FREECAD ASSEMBLY — COMPONENT RECIPES ("Robot")

This assembly document has 5 components, labeled P0..P4 below (a component is one placed body or linked part). 1 of them carries a construction recipe — the FreeCAD feature program that regenerates the part from scratch, quoted from this document or its linked companion documents; the rest are supplied as boundary geometry only. No exploded tour is included for this assembly.
COMPONENT P0 — geometry summary ("DisplayGroup"; no construction recipe available for this part):
  bounding box: 156.0 x 97.0 x 45.0 mm
  tessellated surface: 7,056 triangles
  volume: 191994 mm^3 (28% of its bounding box)
  symmetry: mirror-symmetric across its x mid-plane
COMPONENT P1 — geometry summary ("BodyHolder001"; no construction recipe available for this part):
  bounding box: 90.5 x 83.0 x 64.0 mm
  tessellated surface: 4,908 triangles
  volume: 135069 mm^3 (28% of its bounding box)
  symmetry: mirror-symmetric across its x mid-plane
COMPONENT P2 — geometry summary ("SecondShaft"; no construction recipe available for this part):
  bounding box: 289.3 x 196.0 x 82.9 mm
  tessellated surface: 50,792 triangles
  volume: 322852 mm^3 (7% of its bounding box)
COMPONENT P3 — geometry summary ("RobotBody"; no construction recipe available for this part):
  bounding box: 265.1 x 250.4 x 179.9 mm
  tessellated surface: 350,744 triangles
  volume: 429831 mm^3 (4% of its bounding box)
COMPONENT P4 — recipe-attached ("WoodenChessBoard", a linked part whose construction recipe lives in a companion FreeCAD document of the same project; that document's serialized recipe follows).
Construction recipe (the companion document, serialized — sketch geometry with constraints, then the solid features built on it; lengths are millimeters unless a unit is written):

FCSTD DOCUMENT  (FreeCAD 1.0R39319 (Git))
Label: ChessBoard
License: All rights reserved
LicenseURL: https://en.wikipedia.org/wiki/All_rights_reserved
objects: Sketcher::SketchObject×19, PartDesign::Pocket×10, PartDesign::Pad×8, PartDesign::Body×6, App::LinkGroup×3, App::Link×3, PartDesign::Hole×2, Part::Mirroring×2, Image::ImagePlane×1
note: 106 computed .brp shape members not serialized (recipe doc carries the construction recipe); baked Part::Feature solids carry a one-line shape summary decoded from their .brp
EXTERNAL_REF file=NavigationBoard.FCStd obj=LinkGroup
EXTERNAL_REF file=SnapLock.FCStd obj=LinkGroup
EXTERNAL_REF file=SnapLock.FCStd obj=LinkGroup001

FEATURE [Sketcher::SketchObject] Sketch
  ArcFitTolerance = 1e-06
  AttachmentSupport = -> [XY_Plane]
  FullyConstrained = true
  MakeInternals = false
  MapMode = 5
  sketch-geometry (5):
    g0: LineSegment StartX=-250 StartY=-150 StartZ=0 EndX=250 EndY=-150 EndZ=0
    g1: LineSegment StartX=250 StartY=-150 StartZ=0 EndX=250 EndY=150 EndZ=0
    g2: LineSegment StartX=250 StartY=150 StartZ=0 EndX=-250 EndY=150 EndZ=0
    g3: LineSegment StartX=-250 StartY=150 StartZ=0 EndX=-250 EndY=-150 EndZ=0
    g4: GeomPoint [constr] X=0 Y=0 Z=0
  constraints (12):
    c: Coincident(g0,g1)
    c: Coincident(g1,g2)
    c: Coincident(g2,g3)
    c: Coincident(g3,g0)
    c: Horizontal(g0)
    c: Horizontal(g2)
    c: Vertical(g1)
    c: Vertical(g3)
    c: Symmetric(g2,g0,g4)
    c: Distance(g1,g3) = 500
    c: Distance(g0,g2) = 300
    c: Coincident(g4,g-1)
FEATURE [Image::ImagePlane] ChessBoard
  Placement = pos=(0,0,30) rot=(0,0,1;0rad)
  XSize = 500.127
  YSize = 300.144
FEATURE [PartDesign::Pad] Pad
  Direction = (0,0,1)
  Length = 5
  Length2 = 10
  Profile = -> Sketch
  ReferenceAxis = -> Sketch [N_Axis]
  Refine = true
  Suppressed = false
  Type = 0
FEATURE [Sketcher::SketchObject] Sketch001
  ArcFitTolerance = 1e-06
  AttachmentSupport = -> [XY_Plane001]
  FullyConstrained = true
  MakeInternals = false
  MapMode = 5
  sketch-geometry (5):
    g0: LineSegment StartX=-150 StartY=-150 StartZ=0 EndX=150 EndY=-150 EndZ=0
    g1: LineSegment StartX=150 StartY=-150 StartZ=0 EndX=150 EndY=150 EndZ=0
    g2: LineSegment StartX=150 StartY=150 StartZ=0 EndX=-150 EndY=150 EndZ=0
    g3: LineSegment StartX=-150 StartY=150 StartZ=0 EndX=-150 EndY=-150 EndZ=0
    g4: GeomPoint [constr] X=0 Y=0 Z=0
  constraints (12):
    c: Coincident(g0,g1)
    c: Coincident(g1,g2)
    c: Coincident(g2,g3)
    c: Coincident(g3,g0)
    c: Horizontal(g0)
    c: Horizontal(g2)
    c: Vertical(g1)
    c: Vertical(g3)
    c: Symmetric(g2,g0,g4)
    c: Distance(g1,g3) = 300
    c: Distance(g0,g2) = 300
    c: Coincident(g4,g-1)
FEATURE [PartDesign::Pad] Pad001
  Direction = (0,0,1)
  Length = 5
  Length2 = 10
  Profile = -> Sketch001
  ReferenceAxis = -> Sketch001 [N_Axis]
  Refine = true
  Suppressed = false
  Type = 0
FEATURE [PartDesign::Body] Body001  label="MainBoard"
  AllowCompound = false
  Group = -> [Sketch001,Pad001]
  Origin = -> Origin001
  Placement = pos=(0,0,25) rot=(0,0,1;0rad)
  Tip = -> Pad001
FEATURE [Sketcher::SketchObject] Sketch002
  ArcFitTolerance = 1e-06
  AttachmentSupport = -> [XY_Plane002]
  FullyConstrained = true
  MakeInternals = false
  MapMode = 5
  sketch-geometry (4):
    g0: LineSegment StartX=0 StartY=0 StartZ=0 EndX=0 EndY=-300 EndZ=0
    g1: LineSegment StartX=0 StartY=-300 StartZ=0 EndX=100 EndY=-300 EndZ=0
    g2: LineSegment StartX=100 StartY=-300 StartZ=0 EndX=100 EndY=0 EndZ=0
    g3: LineSegment StartX=100 StartY=0 StartZ=0 EndX=0 EndY=0 EndZ=0
  constraints (11):
    c: Coincident(g0,g1)
    c: Coincident(g1,g2)
    c: Coincident(g2,g3)
    c: Coincident(g3,g0)
    c: Vertical(g0)
    c: Vertical(g2)
    c: Horizontal(g1)
    c: Horizontal(g3)
    c: Distance(g0,g2) = 100
    c: Distance(g1,g3) = 300
    c: Coincident(g0,g-1)
FEATURE [PartDesign::Pad] Pad002
  Direction = (0,0,1)
  Length = 5
  Length2 = 10
  Profile = -> Sketch002
  ReferenceAxis = -> Sketch002 [N_Axis]
  Refine = true
  Suppressed = false
  Type = 0
FEATURE [PartDesign::Body] Body002  label="DropLeft"
  AllowCompound = false
  Group = -> [Sketch002,Pad002]
  Origin = -> Origin002
  Placement = pos=(-250,150,25) rot=(0,0,1;0rad)
  Tip = -> Pad002
FEATURE [Sketcher::SketchObject] Sketch003
  ArcFitTolerance = 1e-06
  AttachmentSupport = -> [XY_Plane003]
  FullyConstrained = true
  MakeInternals = false
  MapMode = 5
  sketch-geometry (4):
    g0: LineSegment StartX=0 StartY=0 StartZ=0 EndX=-100 EndY=0 EndZ=0
    g1: LineSegment StartX=-100 StartY=0 StartZ=0 EndX=-100 EndY=-300 EndZ=0
    g2: LineSegment StartX=-100 StartY=-300 StartZ=0 EndX=0 EndY=-300 EndZ=0
    g3: LineSegment StartX=0 StartY=-300 StartZ=0 EndX=0 EndY=0 EndZ=0
  constraints (11):
    c: Coincident(g0,g1)
    c: Coincident(g1,g2)
    c: Coincident(g2,g3)
    c: Coincident(g3,g0)
    c: Horizontal(g0)
    c: Horizontal(g2)
    c: Vertical(g1)
    c: Vertical(g3)
    c: Distance(g1,g3) = 100
    c: Distance(g0,g2) = 300
    c: Coincident(g0,g-1)
FEATURE [PartDesign::Pad] Pad003
  Direction = (0,0,1)
  Length = 5
  Length2 = 10
  Profile = -> Sketch003
  ReferenceAxis = -> Sketch003 [N_Axis]
  Refine = true
  Suppressed = false
  Type = 0
FEATURE [PartDesign::Body] Body003  label="DropRight"
  AllowCompound = false
  Group = -> [Sketch003,Pad003]
  Origin = -> Origin003
  Placement = pos=(250,150,25) rot=(0,0,1;0rad)
  Tip = -> Pad003
FEATURE [Sketcher::SketchObject] Sketch004
  ArcFitTolerance = 1e-06
  AttachmentSupport = -> [XY_Plane004]
  FullyConstrained = false
  MakeInternals = false
  MapMode = 5
  sketch-geometry (13):
    g0: LineSegment StartX=0 StartY=40 StartZ=0 EndX=0 EndY=0 EndZ=0
    g1: LineSegment StartX=0 StartY=0 StartZ=0 EndX=160 EndY=0 EndZ=0
    g2: LineSegment StartX=0 StartY=40 StartZ=0 EndX=10 EndY=40 EndZ=0
    g3: LineSegment StartX=10 StartY=40 StartZ=0 EndX=10 EndY=30 EndZ=0
    g4: ArcOfCircle CenterX=30 CenterY=30 CenterZ=0 NormalX=0 NormalY=0 NormalZ=1 AngleXU=0 Radius=20 StartAngle=3.14159 EndAngle=4.71239
    g5: LineSegment StartX=90 StartY=42.0946 StartZ=0 EndX=115 EndY=42.0946 EndZ=0
    g6: LineSegment StartX=115 StartY=42.0946 StartZ=0 EndX=115 EndY=25 EndZ=0
    g7: LineSegment StartX=90 StartY=42.0946 StartZ=0 EndX=90 EndY=20 EndZ=0
    g8: LineSegment StartX=30 StartY=10 StartZ=0 EndX=80 EndY=10 EndZ=0
    g9: ArcOfCircle CenterX=125 CenterY=25 CenterZ=0 NormalX=0 NormalY=0 NormalZ=1 AngleXU=0 Radius=10 StartAngle=3.14159 EndAngle=4.71239
    g10: ArcOfCircle CenterX=80 CenterY=20 CenterZ=0 NormalX=0 NormalY=0 NormalZ=1 AngleXU=0 Radius=10 StartAngle=4.71239 EndAngle=6.28319
    g11: LineSegment StartX=125 StartY=15 StartZ=0 EndX=160 EndY=15 EndZ=0
    g12: LineSegment StartX=160 StartY=15 StartZ=0 EndX=160 EndY=0 EndZ=0
  constraints (38):
    c: PointOnObject(g0,g-2)
    c: Coincident(g0,g-1)
    c: Coincident(g0,g1)
    c: Coincident(g0,g2)
    c: Horizontal(g2)
    c: Coincident(g2,g3)
    c: Vertical(g3)
    c: Coincident(g4,g3)
    c: Vertical(g4,g4)
    c: Horizontal(g4,g3)
    c: Radius(g4) = 20
    c: DistanceY(g1,g9) = 15
    c: Distance(g2,g2) = 10
    c: DistanceY(g0,g0) = 40
    c: Horizontal(g5)
    c: Coincident(g5,g6)
    c: Vertical(g6)
    c: Coincident(g5,g7)
    c: Vertical(g7)
    c: Tangent(g4,g8) = -1.5708
    c: Coincident(g9,g6)
    c: Coincident(g10,g7)
    c: Coincident(g10,g8)
    c: Distance(g1,g8) = 10
    c: Radius(g10) = 10
    c: Vertical(g10,g8)
    c: Horizontal(g10,g7)
    c: Radius(g9) = 10
    c: Vertical(g9,g9)
    c: Horizontal(g9,g6)
    c: DistanceX(g-1,g10) = 80
    c: Tangent(g9,g11) = -1.5708
    c: Coincident(g11,g12)
    c: Vertical(g12)
    c: Coincident(g1,g12)
    c: Horizontal(g1)
    c: Distance(g-2,g12) = 160
    c: DistanceX(g5,g5) = 25
FEATURE [PartDesign::Pad] Pad004
  Direction = (0,0,1)
  Length = 29
  Length2 = 10
  Profile = -> Sketch004
  ReferenceAxis = -> Sketch004 [N_Axis]
  Refine = true
  Suppressed = false
  Type = 0
FEATURE [App::LinkGroup] LinkGroup002  label="TopBoard"
  ElementList = -> [Body001,Body002,Body003,ChessBoard]
  LinkMode = 0
  Placement = pos=(0,0,-1) rot=(0,0,1;0rad)
FEATURE [Sketcher::SketchObject] Sketch005
  ArcFitTolerance = 1e-06
  AttachmentSupport = -> [Pad]
  ExternalGeometry = -> [Sketch]
  FullyConstrained = false
  MakeInternals = false
  MapMode = 5
  Placement = pos=(0,0,0) rot=(1,0,0;3.14159rad)
  sketch-geometry (4):
    g0: LineSegment StartX=-92 StartY=-50 StartZ=0 EndX=-92 EndY=-193.39 EndZ=0
    g1: LineSegment StartX=-92 StartY=-193.39 StartZ=0 EndX=92 EndY=-193.39 EndZ=0
    g2: LineSegment StartX=92 StartY=-193.39 StartZ=0 EndX=92 EndY=-50 EndZ=0
    g3: LineSegment StartX=92 StartY=-50 StartZ=0 EndX=-92 EndY=-50 EndZ=0
  constraints (11):
    c: Coincident(g0,g1)
    c: Coincident(g1,g2)
    c: Coincident(g2,g3)
    c: Coincident(g3,g0)
    c: Vertical(g0)
    c: Vertical(g2)
    c: Horizontal(g1)
    c: Horizontal(g3)
    c: Distance(g-2,g2) = 92
    c: Distance(g-2,g0) = 92
    c: Distance(g-3,g3) = 100
FEATURE [PartDesign::Pocket] Pocket
  BaseFeature = -> Pad
  Direction = (0,0,1)
  Length = 5
  Length2 = 5
  Profile = -> Sketch005
  ReferenceAxis = -> Sketch005 [N_Axis]
  Refine = true
  Suppressed = false
  Type = 0
FEATURE [PartDesign::Body] Body  label="Bottom"
  AllowCompound = false
  Group = -> [Sketch,Pad,Sketch005,Pocket]
  Origin = -> Origin
  Tip = -> Pocket
FEATURE [Sketcher::SketchObject] Sketch006
  ArcFitTolerance = 1e-06
  AttachmentSupport = -> [Pad004]
  FullyConstrained = false
  MakeInternals = false
  MapMode = 5
  Placement = pos=(0,0,29) rot=(0,0,1;0rad)
  sketch-geometry (6):
    g0: LineSegment StartX=5 StartY=45 StartZ=0 EndX=5 EndY=5 EndZ=0
    g1: LineSegment StartX=5 StartY=5 StartZ=0 EndX=100 EndY=5 EndZ=0
    g2: LineSegment StartX=275.375 StartY=45 StartZ=0 EndX=5 EndY=45 EndZ=0
    g3: LineSegment StartX=100 StartY=5 StartZ=0 EndX=100 EndY=-8.02974 EndZ=0
    g4: LineSegment StartX=100 StartY=-8.02974 StartZ=0 EndX=275.375 EndY=-8.02974 EndZ=0
    g5: LineSegment StartX=275.375 StartY=45 StartZ=0 EndX=275.375 EndY=-8.02974 EndZ=0
  constraints (16):
    c: Coincident(g0,g1)
    c: Coincident(g2,g0)
    c: Vertical(g0)
    c: Horizontal(g1)
    c: Horizontal(g2)
    c: Distance(g-2,g0) = 5
    c: Distance(g-1,g1) = 5
    c: DistanceY(g0,g0) = 40
    c: Vertical(g3)
    c: Coincident(g3,g4)
    c: Horizontal(g4)
    c: Coincident(g1,g3)
    c: Coincident(g5,g2)
    c: Coincident(g5,g4)
    c: Vertical(g5)
    c: Distance(g-2,g3) = 100
FEATURE [PartDesign::Pocket] Pocket001
  BaseFeature = -> Pad004
  Direction = (0,0,-1)
  Length = 5
  Length2 = 5
  Profile = -> Sketch006
  ReferenceAxis = -> Sketch006 [N_Axis]
  Refine = true
  Suppressed = false
  Type = 0
FEATURE [Sketcher::SketchObject] Sketch007
  ArcFitTolerance = 1e-06
  AttachmentSupport = -> [Pocket001]
  FullyConstrained = false
  MakeInternals = false
  MapMode = 5
  Placement = pos=(0,0,0) rot=(1,0,0;3.14159rad)
  sketch-geometry (6):
    g0: LineSegment StartX=5 StartY=-5 StartZ=0 EndX=5 EndY=-45 EndZ=0
    g1: LineSegment StartX=5 StartY=-45 StartZ=0 EndX=160 EndY=-45 EndZ=0
    g2: LineSegment StartX=45 StartY=-5 StartZ=0 EndX=5 EndY=-5 EndZ=0
    g3: LineSegment StartX=45 StartY=-5 StartZ=0 EndX=45 EndY=8.54607 EndZ=0
    g4: LineSegment StartX=45 StartY=8.54607 StartZ=0 EndX=160 EndY=8.54607 EndZ=0
    g5: LineSegment StartX=160 StartY=8.54607 StartZ=0 EndX=160 EndY=-45 EndZ=0
  constraints (17):
    c: Coincident(g0,g1)
    c: Coincident(g2,g0)
    c: Vertical(g0)
    c: Horizontal(g1)
    c: Horizontal(g2)
    c: Distance(g-1,g2) = 5
    c: Distance(g-2,g0) = 5
    c: DistanceY(g0,g0) = 40
    c: Coincident(g2,g3)
    c: Vertical(g3)
    c: Coincident(g3,g4)
    c: Horizontal(g4)
    c: Coincident(g4,g5)
    c: Coincident(g5,g1)
    c: Vertical(g5)
    c: DistanceX(g0,g2) = 40
    c: Distance(g1,g-2) = 160
FEATURE [PartDesign::Pocket] Pocket002
  BaseFeature = -> Pocket001
  Direction = (0,0,1)
  Length = 5
  Length2 = 5
  Profile = -> Sketch007
  ReferenceAxis = -> Sketch007 [N_Axis]
  Refine = true
  Suppressed = false
  Type = 0
FEATURE [Sketcher::SketchObject] Sketch008
  ArcFitTolerance = 1e-06
  AttachmentSupport = -> [Pocket002]
  ExternalGeometry = -> [Pocket002]
  FullyConstrained = true
  MakeInternals = false
  MapMode = 5
  Placement = pos=(0,0,24) rot=(0,0,1;0rad)
  sketch-geometry (1):
    g0: Circle CenterX=110 CenterY=10 CenterZ=0 NormalX=0 NormalY=0 NormalZ=1 AngleXU=0 Radius=5
  constraints (3):
    c: Diameter(g0) = 10
    c: Distance(g0,g-1) = 10
    c: DistanceX(g-3,g0) = 10
FEATURE [PartDesign::Pocket] Pocket003
  BaseFeature = -> Pocket002
  Direction = (0,0,-1)
  Length = 10
  Length2 = 5
  Profile = -> Sketch008
  ReferenceAxis = -> Sketch008 [N_Axis]
  Refine = true
  Suppressed = false
  Type = 0
FEATURE [Sketcher::SketchObject] Sketch009
  ArcFitTolerance = 1e-06
  AttachmentSupport = -> [XY_Plane005]
  FullyConstrained = false
  MakeInternals = false
  MapMode = 5
  sketch-geometry (13):
    g0: LineSegment StartX=0 StartY=40 StartZ=0 EndX=0 EndY=0 EndZ=0
    g1: LineSegment StartX=0 StartY=0 StartZ=0 EndX=160 EndY=0 EndZ=0
    g2: LineSegment StartX=0 StartY=40 StartZ=0 EndX=10 EndY=40 EndZ=0
    g3: LineSegment StartX=10 StartY=40 StartZ=0 EndX=10 EndY=30 EndZ=0
    g4: ArcOfCircle CenterX=30 CenterY=30 CenterZ=0 NormalX=0 NormalY=0 NormalZ=1 AngleXU=0 Radius=20 StartAngle=3.14159 EndAngle=4.71239
    g5: LineSegment StartX=90 StartY=42.0946 StartZ=0 EndX=115 EndY=42.0946 EndZ=0
    g6: LineSegment StartX=115 StartY=42.0946 StartZ=0 EndX=115 EndY=25 EndZ=0
    g7: LineSegment StartX=90 StartY=42.0946 StartZ=0 EndX=90 EndY=20 EndZ=0
    g8: LineSegment StartX=30 StartY=10 StartZ=0 EndX=80 EndY=10 EndZ=0
    g9: ArcOfCircle CenterX=125 CenterY=25 CenterZ=0 NormalX=0 NormalY=0 NormalZ=1 AngleXU=0 Radius=10 StartAngle=3.14159 EndAngle=4.71239
    g10: ArcOfCircle CenterX=80 CenterY=20 CenterZ=0 NormalX=0 NormalY=0 NormalZ=1 AngleXU=0 Radius=10 StartAngle=4.71239 EndAngle=6.28319
    g11: LineSegment StartX=125 StartY=15 StartZ=0 EndX=160 EndY=15 EndZ=0
    g12: LineSegment StartX=160 StartY=15 StartZ=0 EndX=160 EndY=0 EndZ=0
  constraints (38):
    c: PointOnObject(g0,g-2)
    c: Coincident(g0,g-1)
    c: Coincident(g0,g1)
    c: Coincident(g0,g2)
    c: Horizontal(g2)
    c: Coincident(g2,g3)
    c: Vertical(g3)
    c: Coincident(g4,g3)
    c: Vertical(g4,g4)
    c: Horizontal(g4,g3)
    c: Radius(g4) = 20
    c: DistanceY(g1,g9) = 15
    c: Distance(g2,g2) = 10
    c: DistanceY(g0,g0) = 40
    c: Horizontal(g5)
    c: Coincident(g5,g6)
    c: Vertical(g6)
    c: Coincident(g5,g7)
    c: Vertical(g7)
    c: Tangent(g4,g8) = -1.5708
    c: Coincident(g9,g6)
    c: Coincident(g10,g7)
    c: Coincident(g10,g8)
    c: Distance(g1,g8) = 10
    c: Radius(g10) = 10
    c: Vertical(g10,g8)
    c: Horizontal(g10,g7)
    c: Radius(g9) = 10
    c: Vertical(g9,g9)
    c: Horizontal(g9,g6)
    c: DistanceX(g-1,g10) = 80
    c: Tangent(g9,g11) = -1.5708
    c: Coincident(g11,g12)
    c: Vertical(g12)
    c: Coincident(g1,g12)
    c: Horizontal(g1)
    c: Distance(g-2,g12) = 160
    c: DistanceX(g5,g5) = 25
FEATURE [PartDesign::Pad] Pad005
  Direction = (0,0,1)
  Length = 29
  Length2 = 10
  Profile = -> Sketch009
  ReferenceAxis = -> Sketch009 [N_Axis]
  Refine = true
  Suppressed = false
  Type = 0
FEATURE [Sketcher::SketchObject] Sketch010
  ArcFitTolerance = 1e-06
  AttachmentSupport = -> [Pad005]
  FullyConstrained = false
  MakeInternals = false
  MapMode = 5
  Placement = pos=(0,0,29) rot=(0,0,1;0rad)
  sketch-geometry (6):
    g0: LineSegment StartX=5 StartY=45 StartZ=0 EndX=5 EndY=5 EndZ=0
    g1: LineSegment StartX=5 StartY=5 StartZ=0 EndX=100 EndY=5 EndZ=0
    g2: LineSegment StartX=275.375 StartY=45 StartZ=0 EndX=5 EndY=45 EndZ=0
    g3: LineSegment StartX=100 StartY=5 StartZ=0 EndX=100 EndY=-8.02974 EndZ=0
    g4: LineSegment StartX=100 StartY=-8.02974 StartZ=0 EndX=275.375 EndY=-8.02974 EndZ=0
    g5: LineSegment StartX=275.375 StartY=45 StartZ=0 EndX=275.375 EndY=-8.02974 EndZ=0
  constraints (16):
    c: Coincident(g0,g1)
    c: Coincident(g2,g0)
    c: Vertical(g0)
    c: Horizontal(g1)
    c: Horizontal(g2)
    c: Distance(g-2,g0) = 5
    c: Distance(g-1,g1) = 5
    c: DistanceY(g0,g0) = 40
    c: Vertical(g3)
    c: Coincident(g3,g4)
    c: Horizontal(g4)
    c: Coincident(g1,g3)
    c: Coincident(g5,g2)
    c: Coincident(g5,g4)
    c: Vertical(g5)
    c: Distance(g-2,g3) = 100
FEATURE [PartDesign::Pocket] Pocket004
  BaseFeature = -> Pad005
  Direction = (0,0,-1)
  Length = 5
  Length2 = 5
  Profile = -> Sketch010
  ReferenceAxis = -> Sketch010 [N_Axis]
  Refine = true
  Suppressed = false
  Type = 0
FEATURE [Sketcher::SketchObject] Sketch011
  ArcFitTolerance = 1e-06
  AttachmentSupport = -> [Pocket004]
  FullyConstrained = false
  MakeInternals = false
  MapMode = 5
  Placement = pos=(0,0,0) rot=(1,0,0;3.14159rad)
  sketch-geometry (6):
    g0: LineSegment StartX=5 StartY=-5 StartZ=0 EndX=5 EndY=-45 EndZ=0
    g1: LineSegment StartX=5 StartY=-45 StartZ=0 EndX=160 EndY=-45 EndZ=0
    g2: LineSegment StartX=45 StartY=-5 StartZ=0 EndX=5 EndY=-5 EndZ=0
    g3: LineSegment StartX=45 StartY=-5 StartZ=0 EndX=45 EndY=8.54607 EndZ=0
    g4: LineSegment StartX=45 StartY=8.54607 StartZ=0 EndX=160 EndY=8.54607 EndZ=0
    g5: LineSegment StartX=160 StartY=8.54607 StartZ=0 EndX=160 EndY=-45 EndZ=0
  constraints (17):
    c: Coincident(g0,g1)
    c: Coincident(g2,g0)
    c: Vertical(g0)
    c: Horizontal(g1)
    c: Horizontal(g2)
    c: Distance(g-1,g2) = 5
    c: Distance(g-2,g0) = 5
    c: DistanceY(g0,g0) = 40
    c: Coincident(g2,g3)
    c: Vertical(g3)
    c: Coincident(g3,g4)
    c: Horizontal(g4)
    c: Coincident(g4,g5)
    c: Coincident(g5,g1)
    c: Vertical(g5)
    c: DistanceX(g0,g2) = 40
    c: Distance(g1,g-2) = 160
FEATURE [PartDesign::Pocket] Pocket005
  BaseFeature = -> Pocket004
  Direction = (0,0,1)
  Length = 5
  Length2 = 5
  Profile = -> Sketch011
  ReferenceAxis = -> Sketch011 [N_Axis]
  Refine = true
  Suppressed = false
  Type = 0
FEATURE [Sketcher::SketchObject] Sketch012
  ArcFitTolerance = 1e-06
  AttachmentSupport = -> [Pocket005]
  ExternalGeometry = -> [Pocket005]
  FullyConstrained = true
  MakeInternals = false
  MapMode = 5
  Placement = pos=(0,0,24) rot=(0,0,1;0rad)
  sketch-geometry (1):
    g0: Circle CenterX=110 CenterY=10 CenterZ=0 NormalX=0 NormalY=0 NormalZ=1 AngleXU=0 Radius=5
  constraints (3):
    c: Diameter(g0) = 10
    c: Distance(g0,g-1) = 10
    c: DistanceX(g-3,g0) = 10
FEATURE [PartDesign::Pocket] Pocket006
  BaseFeature = -> Pocket005
  Direction = (0,0,-1)
  Length = 10
  Length2 = 5
  Profile = -> Sketch012
  ReferenceAxis = -> Sketch012 [N_Axis]
  Refine = true
  Suppressed = false
  Type = 0
FEATURE [Sketcher::SketchObject] Sketch013
  ArcFitTolerance = 1e-06
  AttachmentSupport = -> [Pocket006]
  ExternalGeometry = -> [Pocket006]
  FullyConstrained = true
  MakeInternals = false
  MapMode = 5
  Placement = pos=(160,0,0) rot=(0.57735,0.57735,0.57735;2.0944rad)
  sketch-geometry (4):
    g0: LineSegment StartX=15 StartY=24 StartZ=0 EndX=0 EndY=24 EndZ=0
    g1: LineSegment StartX=0 StartY=24 StartZ=0 EndX=0 EndY=15 EndZ=0
    g2: LineSegment StartX=0 StartY=15 StartZ=0 EndX=15 EndY=15 EndZ=0
    g3: LineSegment StartX=15 StartY=15 StartZ=0 EndX=15 EndY=24 EndZ=0
  constraints (11):
    c: Coincident(g0,g1)
    c: Coincident(g1,g2)
    c: Coincident(g2,g3)
    c: Coincident(g3,g0)
    c: Horizontal(g0)
    c: Horizontal(g2)
    c: Vertical(g1)
    c: Vertical(g3)
    c: Coincident(g0,g-3)
    c: PointOnObject(g1,g-2)
    c: Distance(g-1,g2) = 15
FEATURE [PartDesign::Pad] Pad006
  BaseFeature = -> Pocket006
  Direction = (1,0,0)
  Length = 15
  Length2 = 10
  Profile = -> Sketch013
  ReferenceAxis = -> Sketch013 [N_Axis]
  Refine = true
  Suppressed = false
  Type = 0
FEATURE [Sketcher::SketchObject] Sketch014
  ArcFitTolerance = 1e-06
  AttachmentSupport = -> [Pad006]
  ExternalGeometry = -> [Pad006]
  FullyConstrained = true
  MakeInternals = false
  MapMode = 5
  Placement = pos=(0,0,24) rot=(0,0,1;0rad)
  sketch-geometry (1):
    g0: Circle CenterX=167.5 CenterY=7.5 CenterZ=0 NormalX=0 NormalY=0 NormalZ=1 AngleXU=0 Radius=1.75
  constraints (2):
    c: Diameter(g0) = 3.5
    c: Symmetric(g-3,g-4,g0)
FEATURE [PartDesign::Hole] Hole
  BaseFeature = -> Pad006
  CustomThreadClearance = 0
  Depth = 25
  DepthType = 0
  Diameter = 3
  DrillForDepth = false
  DrillPoint = 1
  DrillPointAngle = 118
  HoleCutCountersinkAngle = 90
  HoleCutCustomValues = false
  HoleCutDepth = 0
  HoleCutDiameter = 6.1
  HoleCutType = 0
  ModelThread = false
  Profile = -> Sketch014
  Refine = true
  Suppressed = false
  Tapered = false
  TaperedAngle = 90
  ThreadClass = 0
  ThreadDepth = 25
  ThreadDepthType = 0
  ThreadDirection = 0
  ThreadFit = 0
  ThreadSize = 0
  ThreadType = 0
  Threaded = false
  UseCustomThreadClearance = false
FEATURE [PartDesign::Hole] Hole001
  BaseFeature = -> Hole
  CustomThreadClearance = 0
  Depth = 6
  DepthType = 0
  Diameter = 8
  DrillForDepth = false
  DrillPoint = 0
  DrillPointAngle = 118
  HoleCutCountersinkAngle = 90
  HoleCutCustomValues = false
  HoleCutDepth = 0
  HoleCutDiameter = 6.1
  HoleCutType = 0
  ModelThread = false
  Profile = -> Sketch014
  Refine = true
  Suppressed = false
  Tapered = false
  TaperedAngle = 90
  ThreadClass = 0
  ThreadDepth = 6
  ThreadDepthType = 0
  ThreadDirection = 0
  ThreadFit = 0
  ThreadSize = 0
  ThreadType = 0
  Threaded = false
  UseCustomThreadClearance = false
FEATURE [App::Link] Link  label="NavigationBoard"
  LinkPlacement = pos=(200.5,-84.6001,14) rot=(0,0,1;0rad)
  LinkedObject = -> <external NavigationBoard.FCStd>#LinkGroup
  Placement = pos=(200.5,-84.6001,14) rot=(0,0,1;0rad)
FEATURE [Sketcher::SketchObject] Sketch015
  ArcFitTolerance = 1e-06
  AttachmentSupport = -> [Pocket003]
  ExternalGeometry = -> [Pocket003]
  FullyConstrained = true
  MakeInternals = false
  MapMode = 5
  Placement = pos=(0,0,24) rot=(0,0,1;0rad)
  sketch-geometry (6):
    g0: Circle CenterX=11 CenterY=11 CenterZ=0 NormalX=0 NormalY=0 NormalZ=1 AngleXU=0 Radius=2
    g1: Circle CenterX=94 CenterY=11 CenterZ=0 NormalX=0 NormalY=0 NormalZ=1 AngleXU=0 Radius=2
    g2: Circle CenterX=94 CenterY=36 CenterZ=0 NormalX=0 NormalY=0 NormalZ=1 AngleXU=0 Radius=2
    g3: Circle CenterX=106 CenterY=36 CenterZ=0 NormalX=0 NormalY=0 NormalZ=1 AngleXU=0 Radius=2
    g4: Circle CenterX=124 CenterY=6 CenterZ=0 NormalX=0 NormalY=0 NormalZ=1 AngleXU=0 Radius=2
    g5: Circle CenterX=154 CenterY=6 CenterZ=0 NormalX=0 NormalY=0 NormalZ=1 AngleXU=0 Radius=2
  constraints (18):
    c: Diameter(g0) = 4
    c: Diameter(g1) = 4
    c: Diameter(g2) = 4
    c: Distance(g1,g-3) = 6
    c: Vertical(g2,g1)
    c: Distance(g1,g-5) = 6
    c: DistanceY(g1,g2) = 25
    c: Distance(g0,g-5) = 6
    c: Distance(g0,g-4) = 6
    c: Diameter(g3) = 4
    c: Diameter(g4) = 4
    c: Horizontal(g3,g2)
    c: Distance(g3,g-3) = 6
    c: Distance(g4,g-1) = 6
    c: Distance(g4,g-3) = 24
    c: Diameter(g5) = 4
    c: Distance(g5,g-1) = 6
    c: Distance(g5,g-6) = 6
FEATURE [PartDesign::Pocket] Pocket007
  BaseFeature = -> Pocket003
  Direction = (0,0,-1)
  Length = 5
  Length2 = 5
  Profile = -> Sketch015
  ReferenceAxis = -> Sketch015 [N_Axis]
  Refine = true
  Suppressed = false
  Type = 1
FEATURE [PartDesign::Body] Body004  label="AnchorBL"
  AllowCompound = false
  Group = -> [Sketch004,Pad004,Sketch006,Pocket001,Sketch007,Pocket002,Sketch008,Pocket003,Sketch015,Pocket007]
  Origin = -> Origin004
  Placement = pos=(-250,-150,0) rot=(0,0,1;0rad)
  Tip = -> Pocket007
FEATURE [Part::Mirroring] Part__Mirroring001  label="AnchorBR"
  Base = (0,0,0)
  Normal = (1,0,0)
  Source = -> Body004
FEATURE [Sketcher::SketchObject] Sketch016
  ArcFitTolerance = 1e-06
  AttachmentSupport = -> [Hole001]
  ExternalGeometry = -> [Hole001]
  FullyConstrained = true
  MakeInternals = false
  MapMode = 5
  Placement = pos=(0,0,24) rot=(0,0,1;0rad)
  sketch-geometry (6):
    g0: Circle CenterX=11 CenterY=11 CenterZ=0 NormalX=0 NormalY=0 NormalZ=1 AngleXU=0 Radius=2
    g1: Circle CenterX=94 CenterY=11 CenterZ=0 NormalX=0 NormalY=0 NormalZ=1 AngleXU=0 Radius=2
    g2: Circle CenterX=94 CenterY=36 CenterZ=0 NormalX=0 NormalY=0 NormalZ=1 AngleXU=0 Radius=2
    g3: Circle CenterX=106 CenterY=36 CenterZ=0 NormalX=0 NormalY=0 NormalZ=1 AngleXU=0 Radius=2
    g4: Circle CenterX=124 CenterY=6 CenterZ=0 NormalX=0 NormalY=0 NormalZ=1 AngleXU=0 Radius=2
    g5: Circle CenterX=152 CenterY=6 CenterZ=0 NormalX=0 NormalY=0 NormalZ=1 AngleXU=0 Radius=2
  constraints (18):
    c: Diameter(g0) = 4
    c: Diameter(g1) = 4
    c: Diameter(g2) = 4
    c: Diameter(g3) = 4
    c: Diameter(g4) = 4
    c: Diameter(g5) = 4
    c: Distance(g0,g-3) = 6
    c: Distance(g0,g-4) = 6
    c: DistanceX(g1,g-4) = 6
    c: Distance(g1,g-4) = 6
    c: Vertical(g1,g2)
    c: Horizontal(g3,g2)
    c: DistanceX(g-4,g3) = 6
    c: Distance(g4,g-1) = 6
    c: DistanceX(g-4,g4) = 24
    c: Horizontal(g5,g4)
    c: Distance(g5,g-5) = 8
    c: DistanceY(g1,g2) = 25
FEATURE [PartDesign::Pocket] Pocket008
  BaseFeature = -> Hole001
  Direction = (0,0,-1)
  Length = 5
  Length2 = 5
  Profile = -> Sketch016
  ReferenceAxis = -> Sketch016 [N_Axis]
  Refine = true
  Suppressed = false
  Type = 1
FEATURE [App::Link] Link001  label="LatchesLock"
  LinkPlacement = pos=(100,171,7.49998) rot=(0,1,0;1.5708rad)
  LinkedObject = -> <external SnapLock.FCStd>#LinkGroup
  Placement = pos=(100,171,7.49998) rot=(0,1,0;1.5708rad)
FEATURE [Sketcher::SketchObject] Sketch017
  ArcFitTolerance = 1e-06
  AttachmentSupport = -> [Pocket008]
  ExternalGeometry = -> [Pocket008]
  FullyConstrained = true
  MakeInternals = false
  MapMode = 5
  Placement = pos=(0,0,24) rot=(0,0,1;0rad)
  sketch-geometry (4):
    g0: LineSegment StartX=146 StartY=0 StartZ=0 EndX=146 EndY=-13 EndZ=0
    g1: ArcOfCircle CenterX=150 CenterY=-13 CenterZ=0 NormalX=0 NormalY=0 NormalZ=1 AngleXU=0 Radius=4 StartAngle=3.14159 EndAngle=6.28319
    g2: LineSegment StartX=154 StartY=-13 StartZ=0 EndX=154 EndY=0 EndZ=0
    g3: LineSegment StartX=146 StartY=0 StartZ=0 EndX=154 EndY=0 EndZ=0
  constraints (12):
    c: Vertical(g0)
    c: Coincident(g1,g0)
    c: Radius(g1) = 4
    c: Tangent(g1,g2) = -1.5708
    c: Vertical(g2)
    c: Coincident(g0,g3)
    c: Coincident(g3,g2)
    c: DistanceY(g1,g-1) = 13
    c: Symmetric(g0,g1,g1)
    c: Distance(g2,g-3) = 6
    c: Horizontal(g3)
    c: Horizontal(g2,g-3)
FEATURE [PartDesign::Pad] Pad007
  BaseFeature = -> Pocket008
  Direction = (0,0,1)
  Length = 24
  Length2 = 10
  Profile = -> Sketch017
  ReferenceAxis = -> Sketch017 [N_Axis]
  Refine = true
  Reversed = true
  Suppressed = false
  Type = 0
FEATURE [Sketcher::SketchObject] Sketch018
  ArcFitTolerance = 1e-06
  AttachmentSupport = -> [Pad007]
  FullyConstrained = true
  MakeInternals = false
  MapMode = 5
  Placement = pos=(154,0,0) rot=(0.57735,0.57735,0.57735;2.0944rad)
  sketch-geometry (4):
    g0: LineSegment StartX=0 StartY=15 StartZ=0 EndX=-8 EndY=15 EndZ=0
    g1: LineSegment StartX=-8 StartY=15 StartZ=0 EndX=-8 EndY=5 EndZ=0
    g2: LineSegment StartX=-8 StartY=5 StartZ=0 EndX=0 EndY=5 EndZ=0
    g3: LineSegment StartX=0 StartY=5 StartZ=0 EndX=0 EndY=15 EndZ=0
  constraints (12):
    c: Coincident(g0,g1)
    c: Coincident(g1,g2)
    c: Coincident(g2,g3)
    c: Coincident(g3,g0)
    c: Horizontal(g0)
    c: Horizontal(g2)
    c: Vertical(g1)
    c: Vertical(g3)
    c: Distance(g1,g3) = 8
    c: Distance(g0,g2) = 10
    c: PointOnObject(g0,g-2)
    c: Distance(g-1,g2) = 5
FEATURE [PartDesign::Pocket] Pocket009
  BaseFeature = -> Pad007
  Direction = (-1,0,0)
  Length = 8
  Length2 = 5
  Profile = -> Sketch018
  ReferenceAxis = -> Sketch018 [N_Axis]
  Refine = true
  Suppressed = false
  Type = 0
FEATURE [PartDesign::Body] Body005  label="AnchorTR"
  AllowCompound = false
  Group = -> [Sketch009,Pad005,Sketch010,Pocket004,Sketch011,Pocket005,Sketch012,Pocket006,Sketch013,Pad006,Sketch014,Hole,Hole001,Sketch016,Pocket008,Sketch017,Pad007,Sketch018,Pocket009]
  Origin = -> Origin005
  Placement = pos=(250,150,0) rot=(0,0,1;3.14159rad)
  Tip = -> Pocket009
FEATURE [Part::Mirroring] Part__Mirroring  label="AnchorTL"
  Base = (0,0,0)
  Normal = (1,0,0)
  Source = -> Body005
FEATURE [App::LinkGroup] LinkGroup001  label="Anchors"
  ElementList = -> [Body004,Part__Mirroring001,Body005,Part__Mirroring]
  LinkMode = 0
  Placement = pos=(0,4.76837e-08,9.53674e-07) rot=(0,0,1;0rad)
FEATURE [App::LinkGroup] LinkGroup  label="WoodenChessBoard"
  ElementList = -> [Body,LinkGroup001,LinkGroup002,Link]
  LinkMode = 0
FEATURE [App::Link] Link002  label="LatchesLockRight"
  LinkPlacement = pos=(-100,171,7.5) rot=(0,1,0;1.5708rad)
  LinkedObject = -> <external SnapLock.FCStd>#LinkGroup001
  Placement = pos=(-100,171,7.5) rot=(0,1,0;1.5708rad)
PROVENANCE & LICENSES
A FreeCAD (.FCStd) document from a public repository crawl; recipes are the document's own serialized feature recipes (and, for linked parts, companion documents' recipes).
License: as declared in the source repository (recorded in the dataset sidecar).
